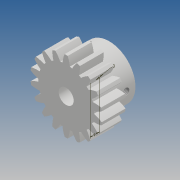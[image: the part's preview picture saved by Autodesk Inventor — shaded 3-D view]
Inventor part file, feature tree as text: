
AUTODESK INVENTOR PART (.ipt)
format: ipt  version: 2017 (Build 210142000, 142)  size: 240,128 bytes
history: native  units: mm
features: other x3, extrude x3, sketch x3, thread x1, pattern_circular x1
ambient origin geometry x8: Origin, YZ Plane, XZ Plane, XY Plane, X Axis, Y Axis, Z Axis, Center Point
bodies: Body1 (feature_tree)
feature tree (11):
  other  "Sólido1"
  extrude  "Extrusión1"  Depth=7.85mm
  sketch  "Boceto2"  dims[d3=3.925mm d4=3.0mm]
  extrude  "Extrusión2"  Depth=3.0mm
  extrude  "Extrusión4"  Depth=10.0mm
  other  "Dientes de engranaje recto3"
  thread  "Rosca1"  [1 undecoded]
  pattern_circular  "Patrón circular2"  [2 undecoded]
  sketch  "Boceto1"  dims[d0=6.3mm d2=7.85mm]
  sketch  "Boceto3"  dims[d5=8.0mm d6=0.0mm d7=3.0mm d10=20.0mm d11=0.0mm d14=10.0mm d15=0.0mm d16=30.0mm d18=360.0deg d26=4.0mm d27=22.0mm d28=10.0mm d29=0.0mm d30=30.0mm d31=360.0deg]
  other  "iFeature1:3"
note: 3 required parameter values undecoded (feature->parameter linkage not recoverable at this tier; creation-order binding heuristic only, values carry confidence <= 0.55)
